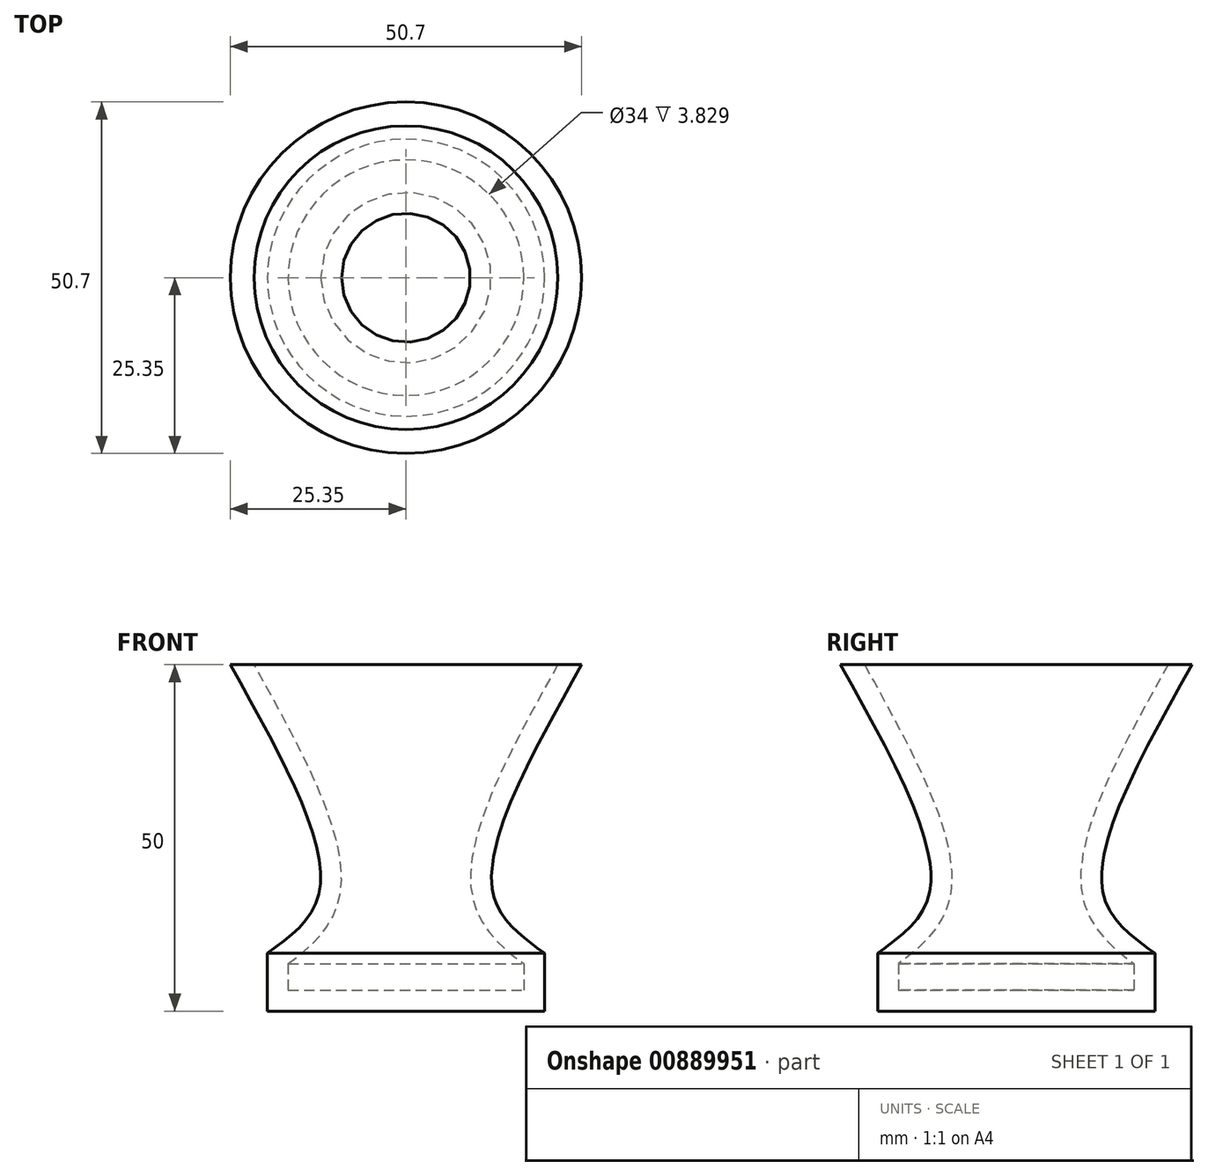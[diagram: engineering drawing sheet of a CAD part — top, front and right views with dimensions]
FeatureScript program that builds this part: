
annotation { "Feature Type Name" : "Feature", "Feature Type Description" : "" }
export const myFeature = defineFeature(function(context is Context, id is Id, definition is map)
    precondition{}
    {
        {
            var Q0;
            Q0=qCreatedBy(makeId("Front.planeOp"),FACE);
            var sketch = newSketch(context, id + "F0", { "sketchPlane" : qUnion([Q0])});
            skLineSegment(sketch, "E0", {"start": v(0, 0) * mm, "end": v(20, 0) * mm});
            skLineSegment(sketch, "E1", {"start": v(0, 0) * mm, "end": v(0, 50) * mm});
            skLineSegment(sketch, "E2", {"start": v(20, 0) * mm, "end": v(20, 8.36) * mm});
            skFitSpline(sketch, "E3", {"points": [v(20, 8.36) * mm, v(12.42, 17.6) * mm, v(25.35, 50) * mm], "startDerivative": vector(-28.1, 20.16) * mm, "endDerivative": vector(33.44, 59.67) * mm});
            skLineSegment(sketch, "E4", {"start": v(0, 50) * mm, "end": v(25.35, 50) * mm});
            skSolve(sketch);
        }
        {
            var Q0;
            Q0=makeQuery(id+"F0.imprint","IMPRINT",FACE,{"disambiguationData":[TD([[makeQuery(id+"F0.imprint","IMPRINT",EDGE,{"derivedFrom":sQuery(id+"F0.wireOp",EDGE,"E0")}),1.0]])]});
            var Q1;
            Q1=sQuery(id+"F0.wireOp",EDGE,"E1");
            revolve(context, id + "F1", {"surfaceOperationType" : NewSurfaceOperationType.NEW, "entities" : qUnion([Q0]), "axis" : qUnion([Q1]), "revolveType" : RevolveType.FULL});
        }
        {
            var Q0;
            Q0=makeQuery(id+"F1.opRevolve","SWEPT_FACE",FACE,{"disambiguationData":[OSD([sQuery(id+"F0.wireOp",EDGE,"E4")])]});
            shell(context, id + "F2", {"entities" : qUnion([Q0]), "thickness" : 3 * mm});
        }
    });
